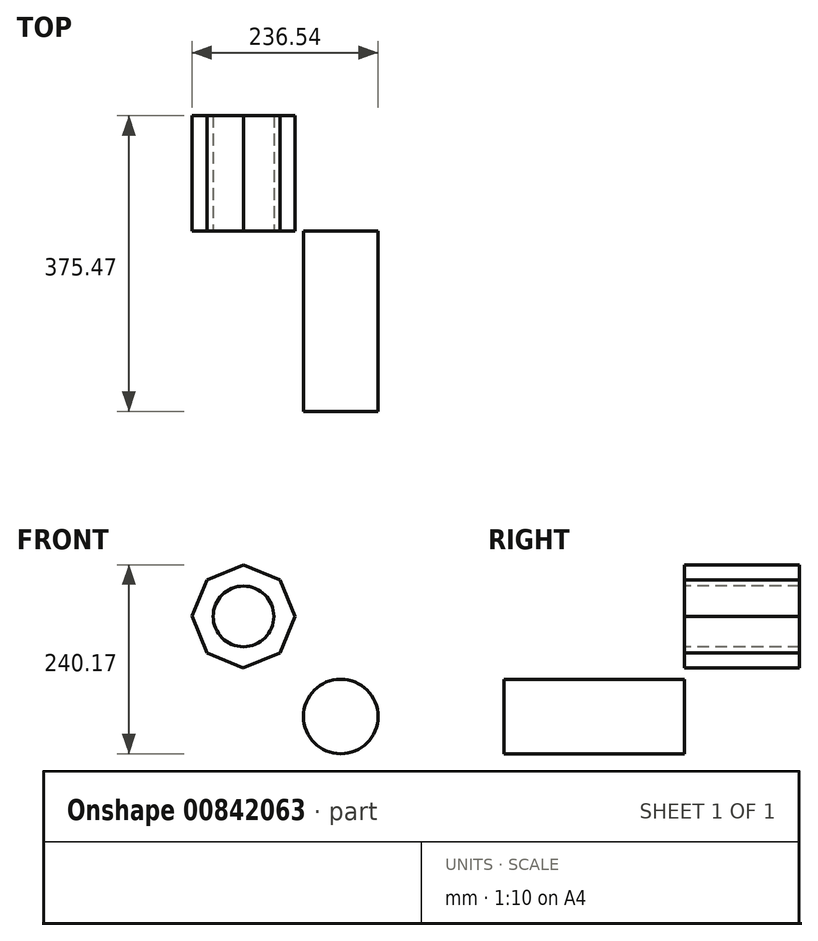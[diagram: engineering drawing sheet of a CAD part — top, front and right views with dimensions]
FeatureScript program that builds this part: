
annotation { "Feature Type Name" : "Feature", "Feature Type Description" : "" }
export const myFeature = defineFeature(function(context is Context, id is Id, definition is map)
    precondition{}
    {
        {
            var Q0;
            Q0=qCreatedBy(makeId("Front.planeOp"),FACE);
            var sketch = newSketch(context, id + "F0", { "sketchPlane" : qUnion([Q0])});
            skCircle(sketch, "E0.cCircle", {"center": v(0, 0) * mm, "radius": 65.59 * mm, "construction": true});
            skLineSegment(sketch, "E0.0", {"start": v(-46.2, 46.56) * mm, "end": v(0.26, 65.59) * mm});
            skLineSegment(sketch, "E0.1", {"start": v(0.26, 65.59) * mm, "end": v(46.56, 46.2) * mm});
            skLineSegment(sketch, "E0.2", {"start": v(46.56, 46.2) * mm, "end": v(65.59, -0.26) * mm});
            skLineSegment(sketch, "E0.3", {"start": v(65.59, -0.26) * mm, "end": v(46.2, -46.56) * mm});
            skLineSegment(sketch, "E0.4", {"start": v(46.2, -46.56) * mm, "end": v(-0.26, -65.59) * mm});
            skLineSegment(sketch, "E0.5", {"start": v(-0.26, -65.59) * mm, "end": v(-46.56, -46.2) * mm});
            skLineSegment(sketch, "E0.6", {"start": v(-46.56, -46.2) * mm, "end": v(-65.59, 0.26) * mm});
            skLineSegment(sketch, "E0.7", {"start": v(-65.59, 0.26) * mm, "end": v(-46.2, 46.56) * mm});
            skSolve(sketch);
        }
        {
            var Q0;
            Q0=qCreatedBy(makeId("Front.planeOp"),FACE);
            var sketch = newSketch(context, id + "F1", { "sketchPlane" : qUnion([Q0])});
            skCircle(sketch, "E1", {"center": v(0, 0) * mm, "radius": 38.5 * mm});
            skSolve(sketch);
        }
        {
            var Q0;
            Q0=qCreatedBy(makeId("Front.planeOp"),FACE);
            var sketch = newSketch(context, id + "F2", { "sketchPlane" : qUnion([Q0])});
            skCircle(sketch, "E2", {"center": v(123.55, -127.18) * mm, "radius": 47.4 * mm});
            skSolve(sketch);
        }
        {
            var Q0;
            Q0=makeQuery(id+"F2.imprint","IMPRINT",FACE,{"disambiguationData":[TD([[makeQuery(id+"F2.imprint","IMPRINT",EDGE,{"derivedFrom":sQuery(id+"F2.wireOp",EDGE,"E2")}),1.0]])]});
            extrude(context, id + "F3", {"entities" : qUnion([Q0]), "depth" : 228.97 * mm, "offsetDistance" : 25.4 * mm});
        }
        {
            var Q0;
            Q0=makeQuery(id+"F1.imprint","IMPRINT",FACE,{"disambiguationData":[TD([[makeQuery(id+"F1.imprint","IMPRINT",EDGE,{"derivedFrom":sQuery(id+"F1.wireOp",EDGE,"E1")}),1.0]])]});
            var Q1;
            Q1=makeQuery(id+"F0.imprint","IMPRINT",FACE,{"disambiguationData":[TD([[makeQuery(id+"F0.imprint","IMPRINT",EDGE,{"derivedFrom":sQuery(id+"F0.wireOp",EDGE,"E0.0")}),-1.0]])]});
            extrude(context, id + "F4", {"entities" : qUnion([Q0, Q1]), "oppositeDirection" : true, "depth" : 146.5 * mm, "offsetDistance" : 25.4 * mm});
        }
    });
